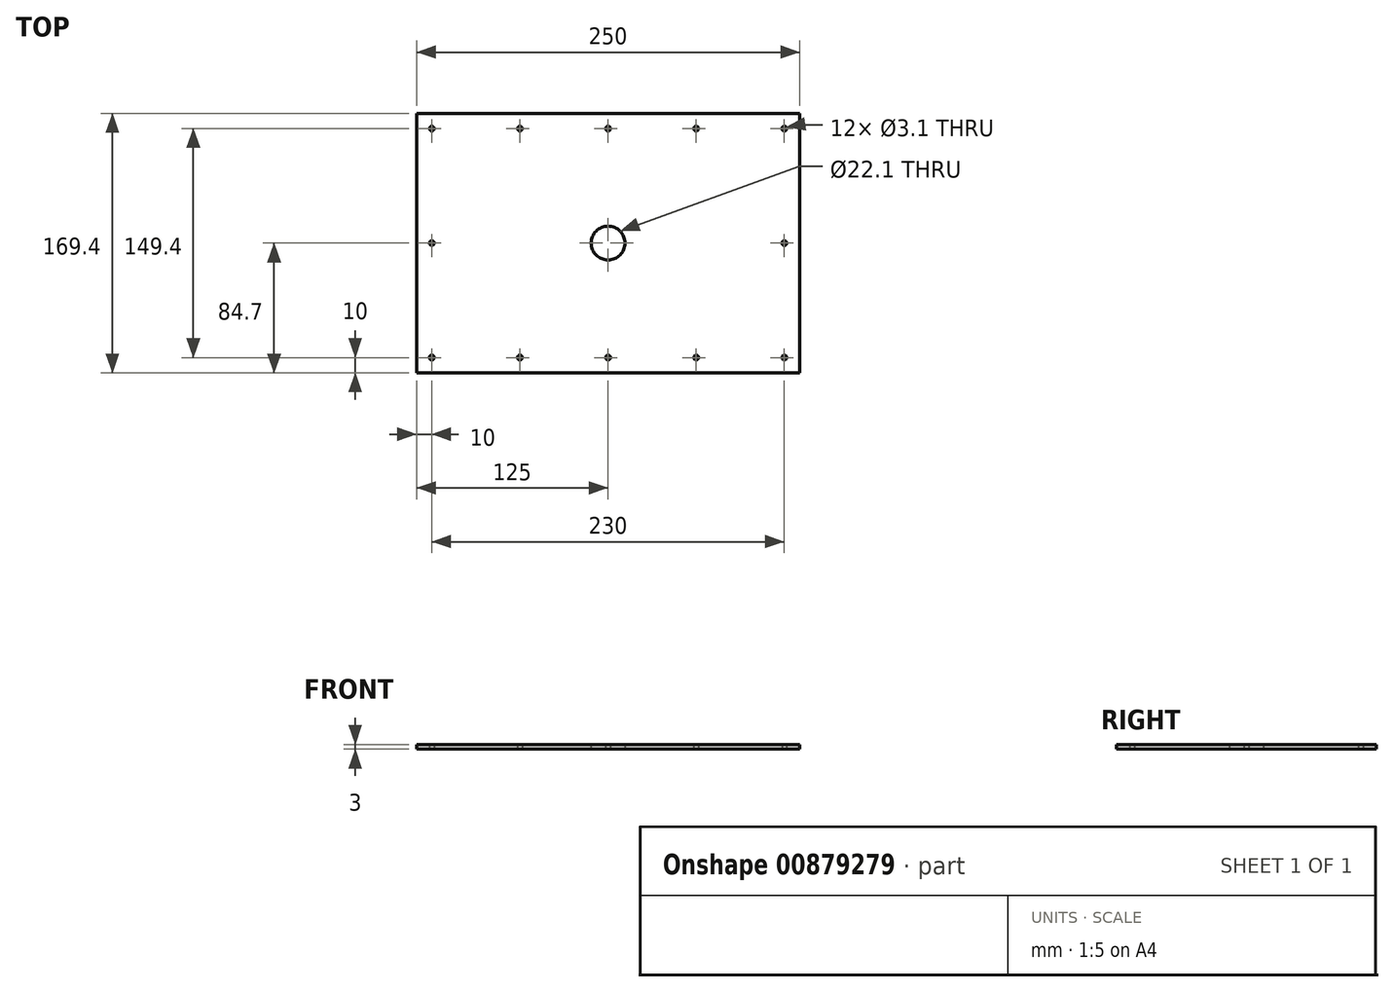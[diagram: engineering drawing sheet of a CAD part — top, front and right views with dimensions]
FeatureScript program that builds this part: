
annotation { "Feature Type Name" : "Feature", "Feature Type Description" : "" }
export const myFeature = defineFeature(function(context is Context, id is Id, definition is map)
    precondition{}
    {
        {
            var Q0;
            Q0=qCreatedBy(makeId("Top.planeOp"),FACE);
            var sketch = newSketch(context, id + "F0", { "sketchPlane" : qUnion([Q0])});
            skLineSegment(sketch, "E0.bottom", {"start": v(0, 0) * mm, "end": v(163, 0) * mm, "construction": true});
            skLineSegment(sketch, "E0.top", {"start": v(0, 129.4) * mm, "end": v(163, 129.4) * mm, "construction": true});
            skLineSegment(sketch, "E0.left", {"start": v(0, 0) * mm, "end": v(0, 129.4) * mm, "construction": true});
            skLineSegment(sketch, "E0.right", {"start": v(163, 0) * mm, "end": v(163, 129.4) * mm, "construction": true});
            skLineSegment(sketch, "E1", {"start": v(0, 129.4) * mm, "end": v(163, 0) * mm, "construction": true});
            skLineSegment(sketch, "E2", {"start": v(163, 129.4) * mm, "end": v(0, 0) * mm, "construction": true});
            skPoint(sketch, "E3", {"position": v(81.5, 64.7) * mm});
            skLineSegment(sketch, "E4.bottom", {"start": v(186.5, 118.2) * mm, "end": v(-23.5, 118.2) * mm, "construction": true});
            skLineSegment(sketch, "E4.top", {"start": v(186.5, 11.2) * mm, "end": v(-23.5, 11.2) * mm, "construction": true});
            skLineSegment(sketch, "E4.left", {"start": v(186.5, 118.2) * mm, "end": v(186.5, 11.2) * mm, "construction": true});
            skLineSegment(sketch, "E4.right", {"start": v(-23.5, 118.2) * mm, "end": v(-23.5, 11.2) * mm, "construction": true});
            skLineSegment(sketch, "E5.bottom", {"start": v(206.5, -20) * mm, "end": v(-43.5, -20) * mm});
            skLineSegment(sketch, "E5.top", {"start": v(206.5, 149.4) * mm, "end": v(-43.5, 149.4) * mm});
            skLineSegment(sketch, "E5.left", {"start": v(206.5, -20) * mm, "end": v(206.5, 149.4) * mm});
            skLineSegment(sketch, "E5.right", {"start": v(-43.5, -20) * mm, "end": v(-43.5, 149.4) * mm});
            skLineSegment(sketch, "E6.0", {"start": v(196.5, 139.4) * mm, "end": v(-33.5, 139.4) * mm});
            skLineSegment(sketch, "E6.1", {"start": v(196.5, -10) * mm, "end": v(196.5, 139.4) * mm});
            skLineSegment(sketch, "E6.2", {"start": v(196.5, -10) * mm, "end": v(-33.5, -10) * mm});
            skLineSegment(sketch, "E6.3", {"start": v(-33.5, -10) * mm, "end": v(-33.5, 139.4) * mm});
            skCircle(sketch, "E7", {"center": v(81.5, 64.7) * mm, "radius": 11.05 * mm});
            skCircle(sketch, "E8", {"center": v(-33.5, 139.4) * mm, "radius": 1.55 * mm});
            skCircle(sketch, "E9", {"center": v(196.5, 139.4) * mm, "radius": 1.55 * mm});
            skCircle(sketch, "E10", {"center": v(196.5, -10) * mm, "radius": 1.55 * mm});
            skCircle(sketch, "E11", {"center": v(-33.5, -10) * mm, "radius": 1.55 * mm});
            skCircle(sketch, "E12", {"center": v(-33.5, 64.7) * mm, "radius": 1.55 * mm});
            skCircle(sketch, "E13", {"center": v(196.5, 64.7) * mm, "radius": 1.55 * mm});
            skCircle(sketch, "E14", {"center": v(81.5, 139.4) * mm, "radius": 1.55 * mm});
            skCircle(sketch, "E15", {"center": v(81.5, -10) * mm, "radius": 1.55 * mm});
            skCircle(sketch, "E16", {"center": v(139, 139.4) * mm, "radius": 1.55 * mm});
            skCircle(sketch, "E17", {"center": v(139, -10) * mm, "radius": 1.55 * mm});
            skCircle(sketch, "E18", {"center": v(24, -10) * mm, "radius": 1.55 * mm});
            skCircle(sketch, "E19", {"center": v(24, 139.4) * mm, "radius": 1.55 * mm});
            skSolve(sketch);
        }
        {
            var Q0;
            Q0=makeQuery(id+"F0.imprint","IMPRINT",FACE,{"disambiguationData":[TD([[makeQuery(id+"F0.imprint","IMPRINT",EDGE,{"derivedFrom":sQuery(id+"F0.wireOp",EDGE,"E5.bottom")}),-1.0]])]});
            var Q1;
            Q1=makeQuery(id+"F0.imprint","IMPRINT",FACE,{"disambiguationData":[TD([[makeQuery(id+"F0.imprint","IMPRINT",EDGE,{"derivedFrom":sQuery(id+"F0.wireOp",EDGE,"E7")}),-1.0]])]});
            extrude(context, id + "F1", {"entities" : qUnion([Q0, Q1]), "depth" : 3 * mm, "offsetDistance" : 25 * mm});
        }
    });
